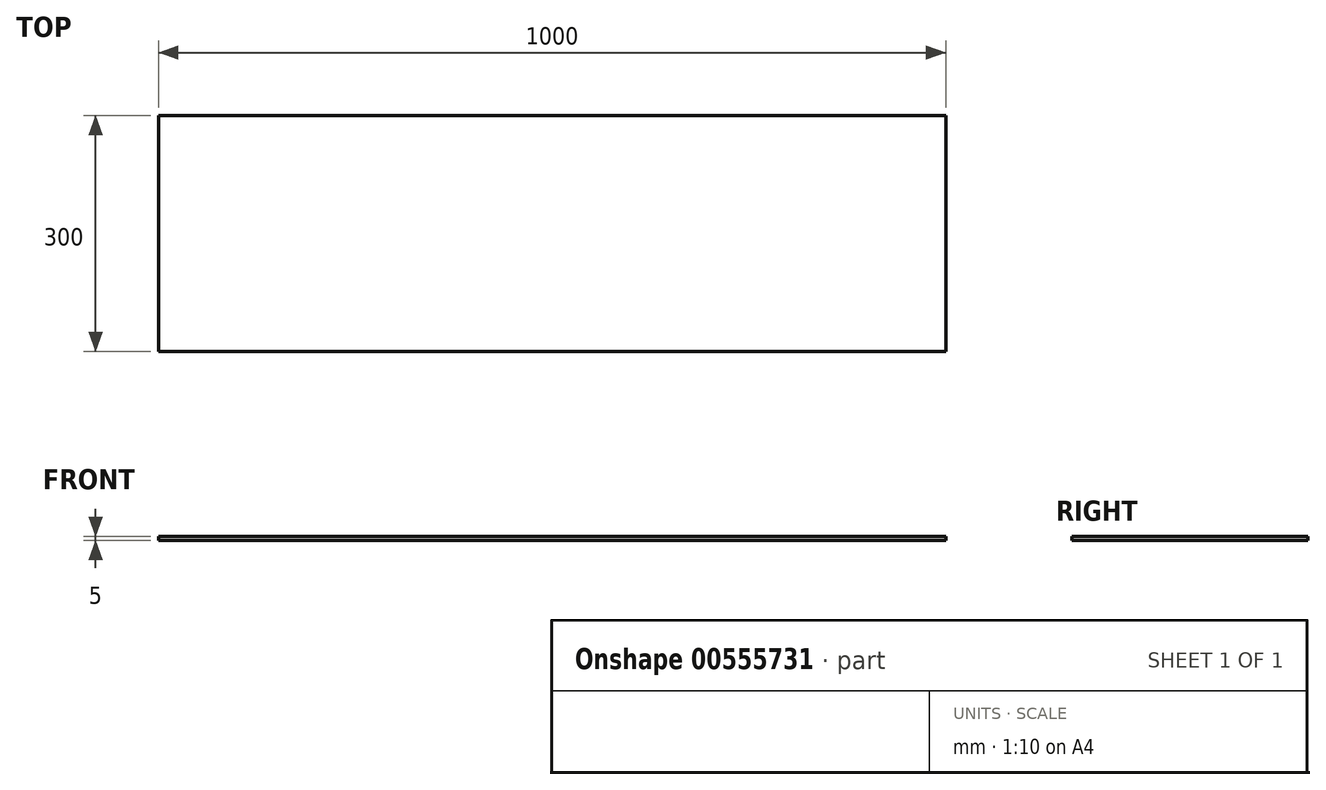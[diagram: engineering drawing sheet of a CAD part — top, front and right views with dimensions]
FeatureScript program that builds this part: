
annotation { "Feature Type Name" : "Feature", "Feature Type Description" : "" }
export const myFeature = defineFeature(function(context is Context, id is Id, definition is map)
    precondition{}
    {
        {
            var Q0;
            Q0=qCreatedBy(makeId("Top.planeOp"),FACE);
            var sketch = newSketch(context, id + "F0", { "sketchPlane" : qUnion([Q0])});
            skLineSegment(sketch, "E0.bottom", {"start": v(500, 150) * mm, "end": v(-500, 150) * mm});
            skLineSegment(sketch, "E0.top", {"start": v(500, -150) * mm, "end": v(-500, -150) * mm});
            skLineSegment(sketch, "E0.left", {"start": v(500, 150) * mm, "end": v(500, -150) * mm});
            skLineSegment(sketch, "E0.right", {"start": v(-500, 150) * mm, "end": v(-500, -150) * mm});
            skPoint(sketch, "E0.middle", {"position": v(0, 0) * mm});
            skSolve(sketch);
        }
        {
            var Q0;
            Q0=makeQuery(id+"F0.imprint","IMPRINT",FACE,{"disambiguationData":[TD([[makeQuery(id+"F0.imprint","IMPRINT",EDGE,{"derivedFrom":sQuery(id+"F0.wireOp",EDGE,"E0.bottom")}),1.0]])]});
            extrude(context, id + "F1", {"entities" : qUnion([Q0]), "depth" : 5 * mm, "offsetDistance" : 25 * mm});
        }
    });
